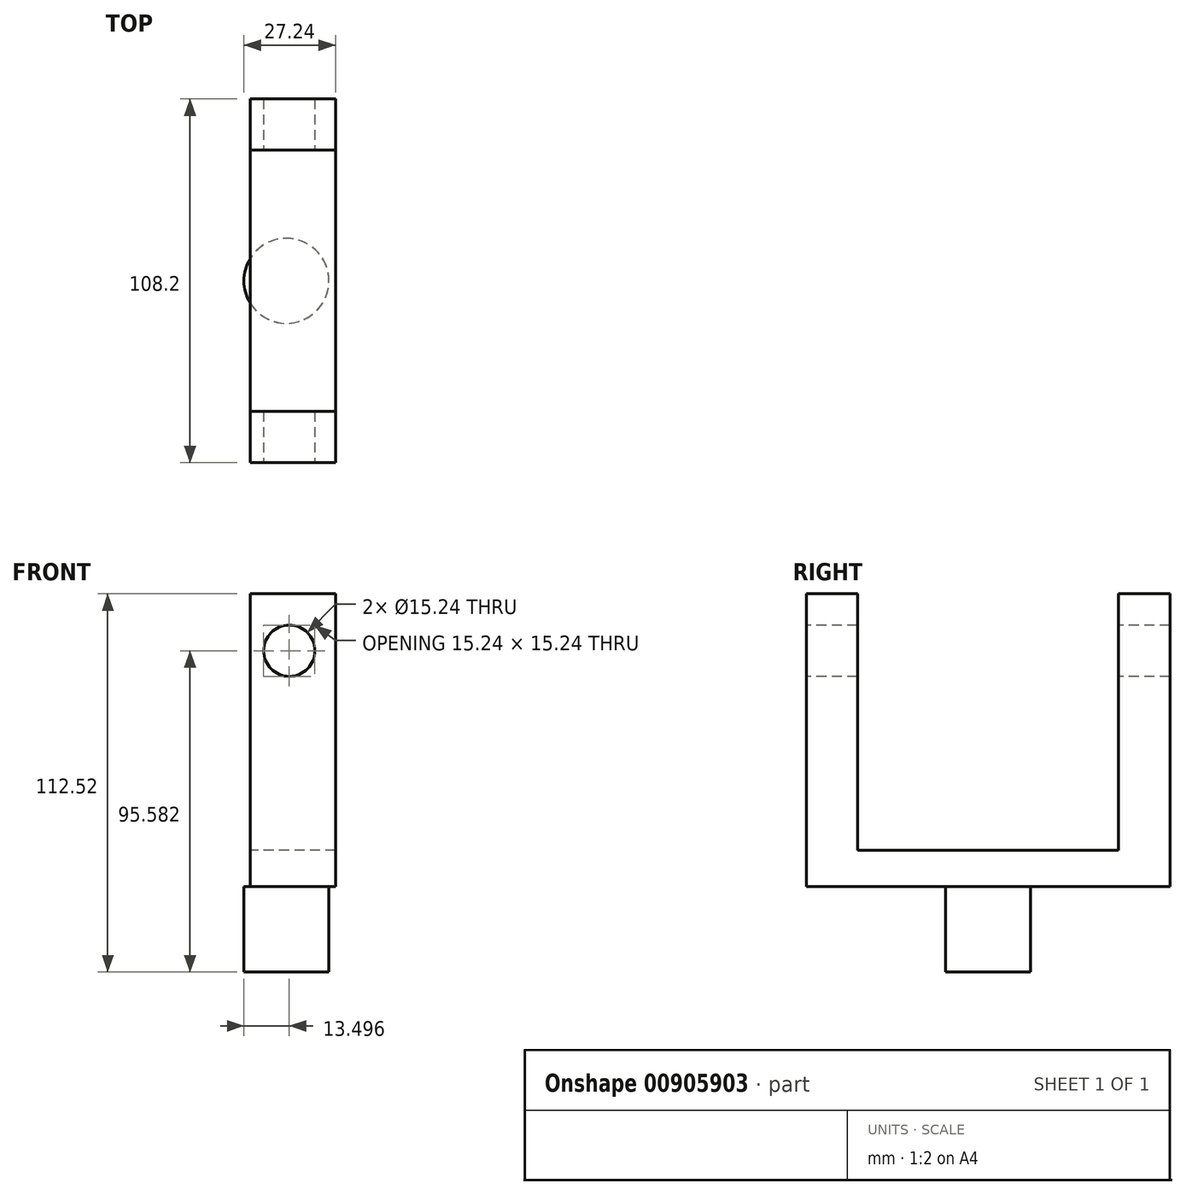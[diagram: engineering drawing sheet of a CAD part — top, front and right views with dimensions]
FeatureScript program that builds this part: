
annotation { "Feature Type Name" : "Feature", "Feature Type Description" : "" }
export const myFeature = defineFeature(function(context is Context, id is Id, definition is map)
    precondition{}
    {
        {
            var Q0;
            Q0=qCreatedBy(makeId("Right.planeOp"),FACE);
            var sketch = newSketch(context, id + "F0", { "sketchPlane" : qUnion([Q0])});
            skLineSegment(sketch, "E0", {"start": v(-64.03, 31.76) * mm, "end": v(-48.8, 31.76) * mm});
            skLineSegment(sketch, "E1", {"start": v(-48.8, 31.76) * mm, "end": v(-48.8, -55.36) * mm});
            skLineSegment(sketch, "E2", {"start": v(-48.8, -55.36) * mm, "end": v(-64.03, -55.36) * mm});
            skLineSegment(sketch, "E3", {"start": v(-64.03, -55.36) * mm, "end": v(-64.03, 31.76) * mm});
            skLineSegment(sketch, "E4", {"start": v(-64.03, -55.36) * mm, "end": v(44.17, -55.36) * mm});
            skLineSegment(sketch, "E5", {"start": v(44.17, -55.36) * mm, "end": v(44.17, 31.76) * mm});
            skLineSegment(sketch, "E6", {"start": v(44.17, 31.76) * mm, "end": v(28.92, 31.76) * mm});
            skLineSegment(sketch, "E7", {"start": v(28.92, 31.76) * mm, "end": v(28.92, -55.36) * mm});
            skLineSegment(sketch, "E8", {"start": v(-48.8, -44.47) * mm, "end": v(28.92, -44.47) * mm});
            skSolve(sketch);
        }
        {
            var Q0;
            {var subQ4=sQuery(id+"F0.wireOp",EDGE,"E8");var subQ12=sQuery(id+"F0.wireOp",EDGE,"E5");var subQ13=sQuery(id+"F0.wireOp",EDGE,"E0");Q0=qUnion([makeQuery(id+"F0.imprint","IMPRINT",FACE,{"disambiguationData":[TD([[makeQuery(id+"F0.imprint","IMPRINT",EDGE,{"derivedFrom":subQ13}),-1.0]])]}),makeQuery(id+"F0.imprint","IMPRINT",FACE,{"disambiguationData":[TD([[makeQuery(id+"F0.imprint","IMPRINT",EDGE,{"derivedFrom":subQ12}),1.0]])]}),makeQuery(id+"F0.imprint","IMPRINT",FACE,{"disambiguationData":[TD([[makeQuery(id+"F0.imprint","IMPRINT",EDGE,{"derivedFrom":subQ4}),-1.0]])]})]);}
            extrude(context, id + "F1", {"entities" : qUnion([Q0]), "depth" : 25.4 * mm, "offsetDistance" : 25.4 * mm});
        }
        {
            var Q0;
            Q0=makeQuery(id+"F1.opExtrude","SWEPT_FACE",FACE,{"disambiguationData":[OSD([sQuery(id+"F0.wireOp",EDGE,"E3")])]});
            var sketch = newSketch(context, id + "F2", { "sketchPlane" : qUnion([Q0])});
            skCircle(sketch, "E9", {"center": v(11.66, 14.82) * mm, "radius": 7.62 * mm});
            skSolve(sketch);
        }
        {
            var Q0;
            Q0=makeQuery(id+"F2.imprint","IMPRINT",FACE,{"disambiguationData":[TD([[makeQuery(id+"F2.imprint","IMPRINT",EDGE,{"derivedFrom":sQuery(id+"F2.wireOp",EDGE,"E9")}),1.0]])]});
            extrude(context, id + "F3", {"entities" : qUnion([Q0]), "operationType" : NewBodyOperationType.REMOVE, "oppositeDirection" : true, "depth" : 127 * mm, "offsetDistance" : 25.4 * mm});
        }
        {
            var Q0;
            Q0=makeQuery(id+"F1.opExtrude","SWEPT_FACE",FACE,{"disambiguationData":[OSD([sQuery(id+"F0.wireOp",EDGE,"E2"),sQuery(id+"F0.wireOp",EDGE,"E4")])]});
            var sketch = newSketch(context, id + "F4", { "sketchPlane" : qUnion([Q0])});
            skCircle(sketch, "E10", {"center": v(10.8, 9.93) * mm, "radius": 12.64 * mm});
            skPoint(sketch, "E10.centerSnap0", {"position": v(25.4, 9.93) * mm});
            skSolve(sketch);
        }
        {
            var Q0;
            Q0 = qSketchRegion(id + "F4", true);
            extrude(context, id + "F5", {"entities" : qUnion([Q0]), "operationType" : NewBodyOperationType.ADD, "depth" : 25.4 * mm, "offsetDistance" : 25.4 * mm});
        }
    });
